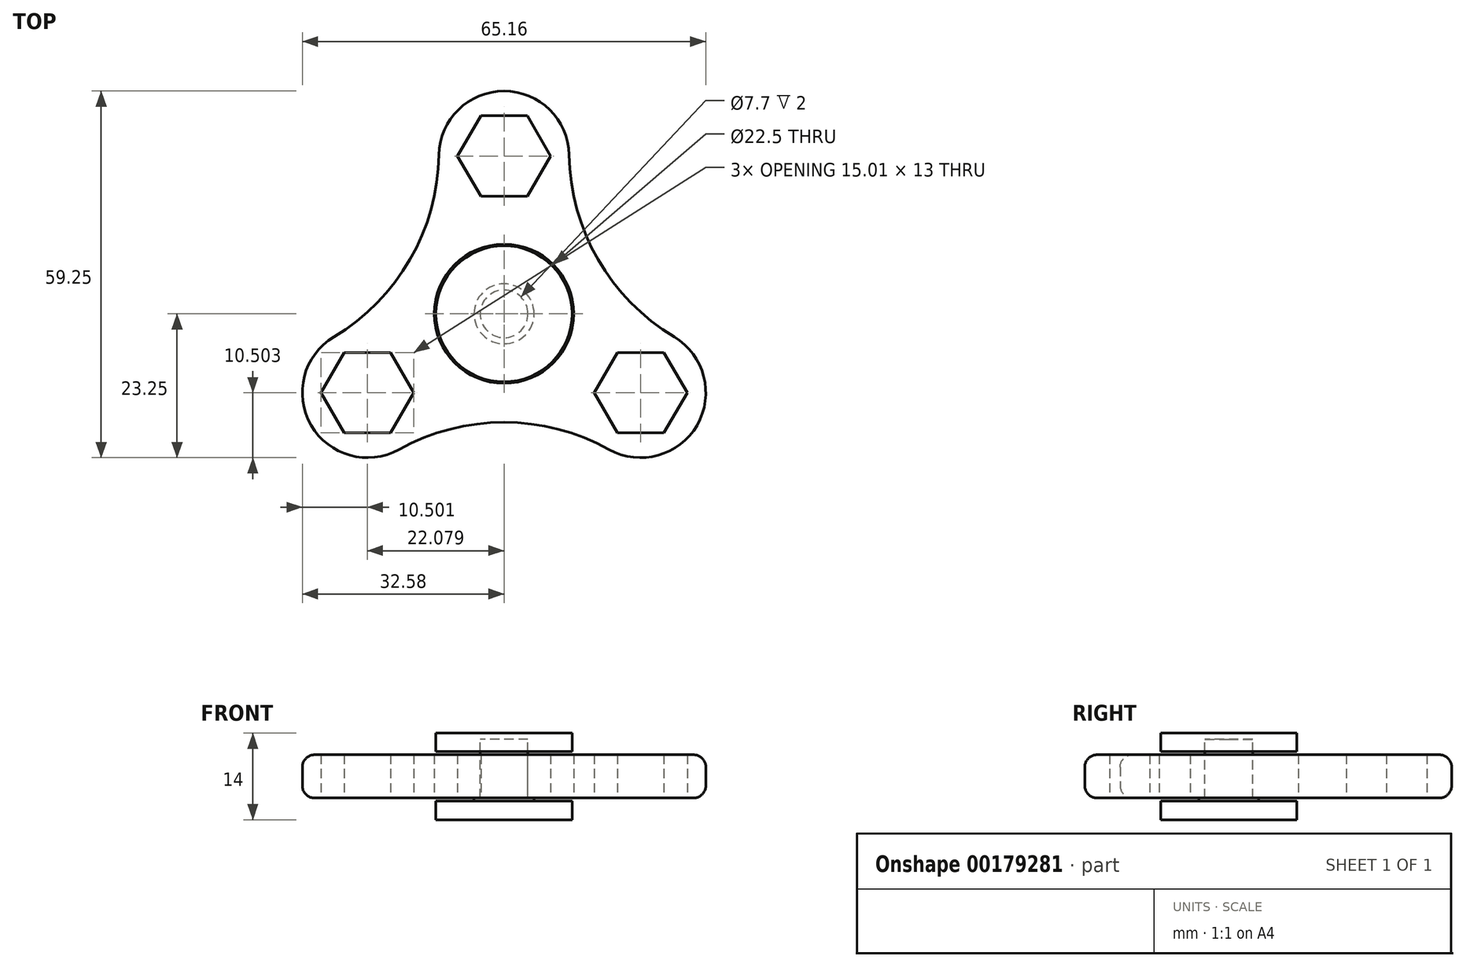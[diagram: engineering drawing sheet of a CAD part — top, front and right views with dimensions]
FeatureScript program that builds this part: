
annotation { "Feature Type Name" : "Feature", "Feature Type Description" : "" }
export const myFeature = defineFeature(function(context is Context, id is Id, definition is map)
    precondition{}
    {
        {
            var Q0;
            Q0=qCreatedBy(makeId("Top.planeOp"),FACE);
            var sketch = newSketch(context, id + "F0", { "sketchPlane" : qUnion([Q0])});
            skCircle(sketch, "E0", {"center": v(0, 0) * mm, "radius": 36 * mm, "construction": true});
            skCircle(sketch, "E1.cCircle", {"center": v(0, 25.5) * mm, "radius": 7.5 * mm, "construction": true});
            skLineSegment(sketch, "E1.0", {"start": v(7.5, 25.5) * mm, "end": v(3.75, 19) * mm});
            skLineSegment(sketch, "E1.1", {"start": v(3.75, 19) * mm, "end": v(-3.75, 19) * mm});
            skLineSegment(sketch, "E1.2", {"start": v(-3.75, 19) * mm, "end": v(-7.5, 25.5) * mm});
            skLineSegment(sketch, "E1.3", {"start": v(-7.5, 25.5) * mm, "end": v(-3.75, 32) * mm});
            skLineSegment(sketch, "E1.4", {"start": v(-3.75, 32) * mm, "end": v(3.75, 32) * mm});
            skLineSegment(sketch, "E1.5", {"start": v(3.75, 32) * mm, "end": v(7.5, 25.5) * mm});
            skCircle(sketch, "E2", {"center": v(0, 25.5) * mm, "radius": 10.5 * mm});
            skCircle(sketch, "E3.1.0", {"center": v(-22.08, -12.75) * mm, "radius": 10.5 * mm});
            skLineSegment(sketch, "E3.1.1", {"start": v(-25.83, -19.25) * mm, "end": v(-29.58, -12.75) * mm});
            skLineSegment(sketch, "E3.1.2", {"start": v(-18.33, -19.25) * mm, "end": v(-25.83, -19.25) * mm});
            skLineSegment(sketch, "E3.1.3", {"start": v(-14.57, -12.75) * mm, "end": v(-18.33, -19.25) * mm});
            skLineSegment(sketch, "E3.1.4", {"start": v(-18.33, -6.25) * mm, "end": v(-14.57, -12.75) * mm});
            skLineSegment(sketch, "E3.1.5", {"start": v(-25.83, -6.25) * mm, "end": v(-18.33, -6.25) * mm});
            skLineSegment(sketch, "E3.1.6", {"start": v(-29.58, -12.75) * mm, "end": v(-25.83, -6.25) * mm});
            skCircle(sketch, "E3.2.0", {"center": v(22.08, -12.75) * mm, "radius": 10.5 * mm});
            skLineSegment(sketch, "E3.2.1", {"start": v(29.58, -12.75) * mm, "end": v(25.83, -19.25) * mm});
            skLineSegment(sketch, "E3.2.2", {"start": v(25.83, -6.25) * mm, "end": v(29.58, -12.75) * mm});
            skLineSegment(sketch, "E3.2.3", {"start": v(18.33, -6.25) * mm, "end": v(25.83, -6.25) * mm});
            skLineSegment(sketch, "E3.2.4", {"start": v(14.57, -12.75) * mm, "end": v(18.33, -6.25) * mm});
            skLineSegment(sketch, "E3.2.5", {"start": v(18.33, -19.25) * mm, "end": v(14.57, -12.75) * mm});
            skLineSegment(sketch, "E3.2.6", {"start": v(25.83, -19.25) * mm, "end": v(18.33, -19.25) * mm});
            skArc(sketch, "E4", {"start": v(10.5, 25.67) * mm, "mid": v(15.19, 8.77) * mm, "end": v(27.49, -3.74) * mm});
            skArc(sketch, "E5.1.0", {"start": v(-27.49, -3.74) * mm, "mid": v(-15.19, 8.77) * mm, "end": v(-10.5, 25.67) * mm});
            skArc(sketch, "E5.2.0", {"start": v(16.98, -21.93) * mm, "mid": v(0, -17.54) * mm, "end": v(-16.98, -21.93) * mm});
            skPoint(sketch, "E6.endSnap0", {"position": v(0, -17.54) * mm});
            skCircle(sketch, "E7", {"center": v(0, 0) * mm, "radius": 11.25 * mm});
            skSolve(sketch);
        }
        {
            var Q0;
            Q0=qSketchRegion(id+"F0",true);
            extrude(context, id + "F1", {"entities" : qUnion([Q0]), "depth" : 7 * mm, "offsetDistance" : 25 * mm});
        }
        {
            var Q0;
            {var subQ0=sQuery(id+"F0.wireOp",EDGE,"E3.1.0");Q0=makeQuery(id+"F1.opExtrude","CAP_EDGE",EDGE,{"disambiguationData":[OSD([subQ0]),TDD([makeQuery(id+"F0.imprint","IMPRINT",EDGE,{"disambiguationData":[TD([[makeQuery(id+"F0.imprint","INTERSECT",VERTEX,{"derivedFrom":[subQ0,sQuery(id+"F0.wireOp",EDGE,"E5.1.0")]}),-1.0]])],"derivedFrom":subQ0})])],"isStart":false});}
            var Q1;
            {var subQ0=sQuery(id+"F0.wireOp",EDGE,"E3.1.0");Q1=makeQuery(id+"F1.opExtrude","CAP_EDGE",EDGE,{"disambiguationData":[OSD([subQ0]),TDD([makeQuery(id+"F0.imprint","IMPRINT",EDGE,{"disambiguationData":[TD([[makeQuery(id+"F0.imprint","INTERSECT",VERTEX,{"derivedFrom":[subQ0,sQuery(id+"F0.wireOp",EDGE,"E5.1.0")]}),-1.0]])],"derivedFrom":subQ0})])],"isStart":true});}
            fillet(context, id + "F2", {"entities" : qUnion([Q0, Q1]), "radius" : 2 * mm, "tangentPropagation" : true, "allowEdgeOverflow" : false});
        }
        {
            var Q0;
            Q0=qCreatedBy(makeId("Right.planeOp"),FACE);
            var sketch = newSketch(context, id + "F3", { "sketchPlane" : qUnion([Q0])});
            skLineSegment(sketch, "E8.bottom", {"start": v(-3.85, 7) * mm, "end": v(-3.95, 7) * mm});
            skLineSegment(sketch, "E8.top", {"start": v(-3.85, 0) * mm, "end": v(-3.95, 0) * mm});
            skLineSegment(sketch, "E8.left", {"start": v(-3.85, 7) * mm, "end": v(-3.85, 0) * mm});
            skLineSegment(sketch, "E8.right", {"start": v(-3.95, 7) * mm, "end": v(-3.95, 0) * mm});
            skLineSegment(sketch, "E9", {"start": v(0, 14.83) * mm, "end": v(0, -7.53) * mm, "construction": true});
            skLineSegment(sketch, "E10", {"start": v(0, 9.5) * mm, "end": v(-3.85, 9.5) * mm});
            skLineSegment(sketch, "E11", {"start": v(-3.85, 9.5) * mm, "end": v(-3.85, 0) * mm});
            skLineSegment(sketch, "E12", {"start": v(-3.85, 0) * mm, "end": v(-4.85, 0) * mm});
            skLineSegment(sketch, "E13", {"start": v(-4.85, 0) * mm, "end": v(-4.85, -0.5) * mm});
            skLineSegment(sketch, "E14", {"start": v(-4.85, -0.5) * mm, "end": v(-11, -0.5) * mm});
            skLineSegment(sketch, "E15", {"start": v(-11, -0.5) * mm, "end": v(-11, -3.5) * mm});
            skLineSegment(sketch, "E16", {"start": v(-11, -3.5) * mm, "end": v(0, -3.5) * mm});
            skLineSegment(sketch, "E17", {"start": v(0, -3.5) * mm, "end": v(0, 9.5) * mm});
            skLineSegment(sketch, "E18", {"start": v(0, 10.5) * mm, "end": v(-11, 10.5) * mm});
            skLineSegment(sketch, "E19", {"start": v(-11, 10.5) * mm, "end": v(-11, 7.5) * mm});
            skLineSegment(sketch, "E20", {"start": v(-3.85, 7.5) * mm, "end": v(-11, 7.5) * mm});
            skLineSegment(sketch, "E21", {"start": v(-3.85, 7.5) * mm, "end": v(-3.85, 9.5) * mm});
            skLineSegment(sketch, "E22", {"start": v(-3.85, 9.5) * mm, "end": v(0, 9.5) * mm});
            skLineSegment(sketch, "E23", {"start": v(0, 9.5) * mm, "end": v(0, 10.5) * mm});
            skSolve(sketch);
        }
        {
            var Q0;
            {var subQ0=sQuery(id+"F3.wireOp",EDGE,"E12");Q0=makeQuery(id+"F3.imprint","IMPRINT",FACE,{"disambiguationData":[TD([[makeQuery(id+"F3.imprint","IMPRINT",EDGE,{"derivedFrom":subQ0}),1.0]])]});}
            var Q1;
            Q1=sQuery(id+"F3.wireOp",EDGE,"E9");
            revolve(context, id + "F4", {"surfaceOperationType" : NewSurfaceOperationType.NEW, "entities" : qUnion([Q0]), "axis" : qUnion([Q1]), "revolveType" : RevolveType.FULL});
        }
        {
            var Q0;
            Q0=makeQuery(id+"F3.imprint","IMPRINT",FACE,{"disambiguationData":[TD([[makeQuery(id+"F3.imprint","IMPRINT",EDGE,{"derivedFrom":sQuery(id+"F3.wireOp",EDGE,"E18")}),1.0]])]});
            var Q1;
            Q1=sQuery(id+"F3.wireOp",EDGE,"E9");
            revolve(context, id + "F5", {"surfaceOperationType" : NewSurfaceOperationType.NEW, "entities" : qUnion([Q0]), "axis" : qUnion([Q1]), "revolveType" : RevolveType.FULL});
        }
    });
